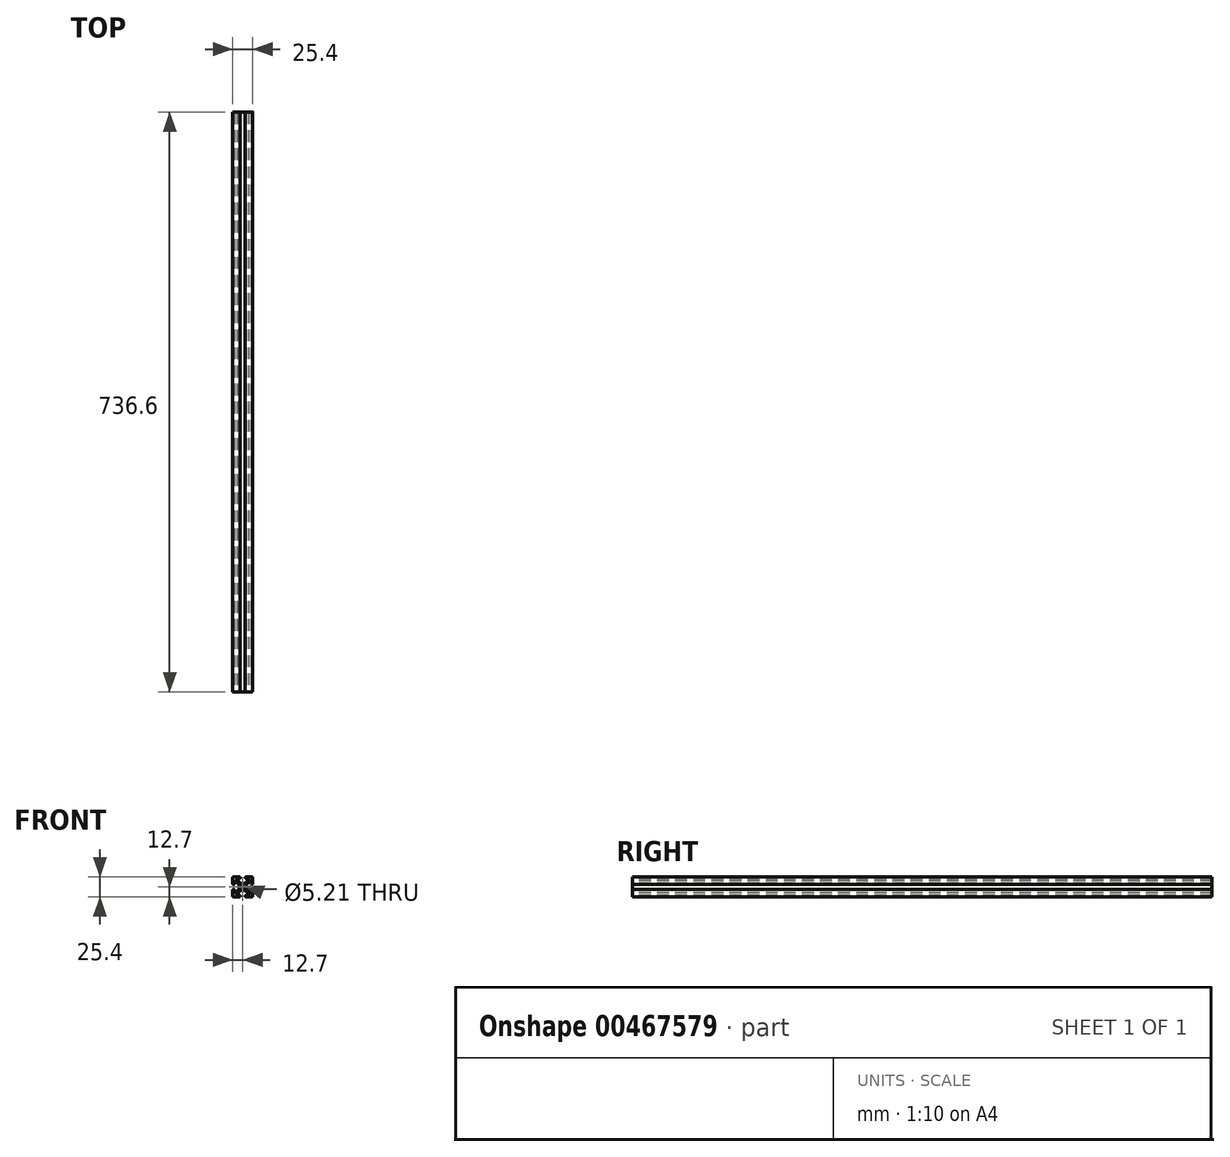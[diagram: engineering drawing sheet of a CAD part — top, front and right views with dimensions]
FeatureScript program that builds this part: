
annotation { "Feature Type Name" : "Feature", "Feature Type Description" : "" }
export const myFeature = defineFeature(function(context is Context, id is Id, definition is map)
    precondition{}
    {
        {
            var Q0;
            Q0=qCreatedBy(makeId("Front.planeOp"),FACE);
            var sketch = newSketch(context, id + "F0", { "sketchPlane" : qUnion([Q0])});
            skLineSegment(sketch, "E0", {"start": v(0, 0) * mm, "end": v(0, 4.5) * mm});
            skLineSegment(sketch, "E1", {"start": v(0, 4.5) * mm, "end": v(-2.54, 4.5) * mm});
            skLineSegment(sketch, "E2", {"start": v(-3.31, 4.83) * mm, "end": v(-7.1, 8.63) * mm});
            skLineSegment(sketch, "E3", {"start": v(-6.34, 10.5) * mm, "end": v(-4.33, 10.5) * mm});
            skLineSegment(sketch, "E4", {"start": v(-3.24, 11.58) * mm, "end": v(-3.24, 11.6) * mm});
            skLineSegment(sketch, "E5", {"start": v(-4.33, 12.7) * mm, "end": v(-11.6, 12.7) * mm});
            skLineSegment(sketch, "E6", {"start": v(-12.7, 11.6) * mm, "end": v(-12.7, 4.34) * mm});
            skLineSegment(sketch, "E7", {"start": v(-11.6, 3.25) * mm, "end": v(-11.58, 3.25) * mm});
            skLineSegment(sketch, "E8", {"start": v(-10.5, 4.34) * mm, "end": v(-10.5, 6.24) * mm});
            skLineSegment(sketch, "E9", {"start": v(-8.63, 7.02) * mm, "end": v(-4.83, 3.22) * mm});
            skLineSegment(sketch, "E10", {"start": v(-4.5, 2.45) * mm, "end": v(-4.5, 0) * mm});
            skLineSegment(sketch, "E11", {"start": v(-4.5, 0) * mm, "end": v(0, 0) * mm});
            skPoint(sketch, "E12.visualSharp", {"position": v(-12.7, 12.7) * mm});
            skArc(sketch, "E12.filletArc", {"start": v(-11.6, 12.7) * mm, "mid": v(-12.38, 12.38) * mm, "end": v(-12.7, 11.6) * mm});
            skPoint(sketch, "E13.visualSharp", {"position": v(-10.5, 3.25) * mm});
            skArc(sketch, "E13.filletArc", {"start": v(-11.58, 3.25) * mm, "mid": v(-10.81, 3.57) * mm, "end": v(-10.5, 4.34) * mm});
            skPoint(sketch, "E14.visualSharp", {"position": v(-12.7, 3.25) * mm});
            skArc(sketch, "E14.filletArc", {"start": v(-12.7, 4.34) * mm, "mid": v(-12.38, 3.57) * mm, "end": v(-11.6, 3.25) * mm});
            skPoint(sketch, "E15.visualSharp", {"position": v(-3.24, 10.5) * mm});
            skArc(sketch, "E15.filletArc", {"start": v(-4.33, 10.5) * mm, "mid": v(-3.56, 10.81) * mm, "end": v(-3.24, 11.58) * mm});
            skPoint(sketch, "E16.visualSharp", {"position": v(-3.24, 12.7) * mm});
            skArc(sketch, "E16.filletArc", {"start": v(-3.24, 11.6) * mm, "mid": v(-3.56, 12.38) * mm, "end": v(-4.33, 12.7) * mm});
            skPoint(sketch, "E17.visualSharp", {"position": v(-8.97, 10.5) * mm});
            skArc(sketch, "E17.filletArc", {"start": v(-6.34, 10.5) * mm, "mid": v(-7.35, 9.82) * mm, "end": v(-7.1, 8.63) * mm});
            skPoint(sketch, "E18.visualSharp", {"position": v(-10.5, 8.88) * mm});
            skArc(sketch, "E18.filletArc", {"start": v(-8.63, 7.02) * mm, "mid": v(-9.82, 7.25) * mm, "end": v(-10.5, 6.24) * mm});
            skPoint(sketch, "E19.visualSharp", {"position": v(-4.5, 2.9) * mm});
            skArc(sketch, "E19.filletArc", {"start": v(-4.5, 2.45) * mm, "mid": v(-4.6, 2.87) * mm, "end": v(-4.83, 3.22) * mm});
            skPoint(sketch, "E20.visualSharp", {"position": v(-3, 4.5) * mm});
            skArc(sketch, "E20.filletArc", {"start": v(-3.31, 4.83) * mm, "mid": v(-2.96, 4.6) * mm, "end": v(-2.54, 4.5) * mm});
            skLineSegment(sketch, "E21.MirrorCS", {"start": v(3.24, 11.58) * mm, "end": v(3.24, 11.6) * mm});
            skArc(sketch, "E22.MirrorCS", {"start": v(12.7, 4.34) * mm, "mid": v(12.38, 3.57) * mm, "end": v(11.6, 3.25) * mm});
            skArc(sketch, "E23.MirrorCS", {"start": v(4.33, 10.5) * mm, "mid": v(3.56, 10.81) * mm, "end": v(3.24, 11.58) * mm});
            skLineSegment(sketch, "E24.MirrorCS", {"start": v(11.6, 3.25) * mm, "end": v(11.58, 3.25) * mm});
            skArc(sketch, "E25.MirrorCS", {"start": v(3.31, 4.83) * mm, "mid": v(2.96, 4.6) * mm, "end": v(2.54, 4.5) * mm});
            skArc(sketch, "E26.MirrorCS", {"start": v(4.5, 2.45) * mm, "mid": v(4.6, 2.87) * mm, "end": v(4.83, 3.22) * mm});
            skArc(sketch, "E27.MirrorCS", {"start": v(11.58, 3.25) * mm, "mid": v(10.81, 3.57) * mm, "end": v(10.5, 4.34) * mm});
            skArc(sketch, "E28.MirrorCS", {"start": v(3.24, 11.6) * mm, "mid": v(3.56, 12.38) * mm, "end": v(4.33, 12.7) * mm});
            skArc(sketch, "E29.MirrorCS", {"start": v(11.6, 12.7) * mm, "mid": v(12.38, 12.38) * mm, "end": v(12.7, 11.6) * mm});
            skArc(sketch, "E30.MirrorCS", {"start": v(8.63, 7.02) * mm, "mid": v(9.82, 7.25) * mm, "end": v(10.5, 6.24) * mm});
            skLineSegment(sketch, "E31.MirrorCS", {"start": v(4.5, 2.45) * mm, "end": v(4.5, 0) * mm});
            skLineSegment(sketch, "E32.MirrorCS", {"start": v(10.5, 4.34) * mm, "end": v(10.5, 6.24) * mm});
            skArc(sketch, "E33.MirrorCS", {"start": v(6.34, 10.5) * mm, "mid": v(7.35, 9.82) * mm, "end": v(7.1, 8.63) * mm});
            skLineSegment(sketch, "E34.MirrorCS", {"start": v(0, 4.5) * mm, "end": v(2.54, 4.5) * mm});
            skLineSegment(sketch, "E35.MirrorCS", {"start": v(6.34, 10.5) * mm, "end": v(4.33, 10.5) * mm});
            skLineSegment(sketch, "E36.MirrorCS", {"start": v(4.33, 12.7) * mm, "end": v(11.6, 12.7) * mm});
            skPoint(sketch, "E37.MirrorP", {"position": v(12.7, 3.25) * mm});
            skLineSegment(sketch, "E38.MirrorCS", {"start": v(4.5, 0) * mm, "end": v(0, 0) * mm});
            skPoint(sketch, "E39.MirrorP", {"position": v(12.7, 12.7) * mm});
            skPoint(sketch, "E40.MirrorP", {"position": v(3, 4.5) * mm});
            skPoint(sketch, "E41.MirrorP", {"position": v(10.5, 3.25) * mm});
            skLineSegment(sketch, "E42.MirrorCS", {"start": v(8.63, 7.02) * mm, "end": v(4.83, 3.22) * mm});
            skPoint(sketch, "E43.MirrorP", {"position": v(3.24, 10.5) * mm});
            skLineSegment(sketch, "E44.MirrorCS", {"start": v(12.7, 11.6) * mm, "end": v(12.7, 4.34) * mm});
            skPoint(sketch, "E45.MirrorP", {"position": v(4.5, 2.9) * mm});
            skPoint(sketch, "E46.MirrorP", {"position": v(10.5, 8.88) * mm});
            skPoint(sketch, "E47.MirrorP", {"position": v(8.97, 10.5) * mm});
            skPoint(sketch, "E48.MirrorP", {"position": v(3.24, 12.7) * mm});
            skLineSegment(sketch, "E49.MirrorCS", {"start": v(3.31, 4.83) * mm, "end": v(7.1, 8.63) * mm});
            skLineSegment(sketch, "E50.MirrorCS", {"start": v(-3.24, -11.58) * mm, "end": v(-3.24, -11.6) * mm});
            skArc(sketch, "E51.MirrorCS", {"start": v(-3.24, -11.6) * mm, "mid": v(-3.56, -12.38) * mm, "end": v(-4.33, -12.7) * mm});
            skArc(sketch, "E52.MirrorCS", {"start": v(-4.33, -10.5) * mm, "mid": v(-3.56, -10.81) * mm, "end": v(-3.24, -11.58) * mm});
            skLineSegment(sketch, "E53.MirrorCS", {"start": v(3.24, -11.58) * mm, "end": v(3.24, -11.6) * mm});
            skArc(sketch, "E54.MirrorCS", {"start": v(3.24, -11.6) * mm, "mid": v(3.56, -12.38) * mm, "end": v(4.33, -12.7) * mm});
            skLineSegment(sketch, "E55.MirrorCS", {"start": v(11.6, -3.25) * mm, "end": v(11.58, -3.25) * mm});
            skLineSegment(sketch, "E56.MirrorCS", {"start": v(0, -4.5) * mm, "end": v(2.54, -4.5) * mm});
            skArc(sketch, "E57.MirrorCS", {"start": v(-3.31, -4.83) * mm, "mid": v(-2.96, -4.6) * mm, "end": v(-2.54, -4.5) * mm});
            skArc(sketch, "E58.MirrorCS", {"start": v(12.7, -4.34) * mm, "mid": v(12.38, -3.57) * mm, "end": v(11.6, -3.25) * mm});
            skArc(sketch, "E59.MirrorCS", {"start": v(3.31, -4.83) * mm, "mid": v(2.96, -4.6) * mm, "end": v(2.54, -4.5) * mm});
            skArc(sketch, "E60.MirrorCS", {"start": v(11.58, -3.25) * mm, "mid": v(10.81, -3.57) * mm, "end": v(10.5, -4.34) * mm});
            skLineSegment(sketch, "E61.MirrorCS", {"start": v(-11.6, -3.25) * mm, "end": v(-11.58, -3.25) * mm});
            skLineSegment(sketch, "E62.MirrorCS", {"start": v(0, -4.5) * mm, "end": v(-2.54, -4.5) * mm});
            skArc(sketch, "E63.MirrorCS", {"start": v(-12.7, -4.34) * mm, "mid": v(-12.38, -3.57) * mm, "end": v(-11.6, -3.25) * mm});
            skArc(sketch, "E64.MirrorCS", {"start": v(-11.58, -3.25) * mm, "mid": v(-10.81, -3.57) * mm, "end": v(-10.5, -4.34) * mm});
            skArc(sketch, "E65.MirrorCS", {"start": v(-4.5, -2.45) * mm, "mid": v(-4.6, -2.87) * mm, "end": v(-4.83, -3.22) * mm});
            skArc(sketch, "E66.MirrorCS", {"start": v(4.5, -2.45) * mm, "mid": v(4.6, -2.87) * mm, "end": v(4.83, -3.22) * mm});
            skLineSegment(sketch, "E67.MirrorCS", {"start": v(10.5, -4.34) * mm, "end": v(10.5, -6.24) * mm});
            skArc(sketch, "E68.MirrorCS", {"start": v(-8.63, -7.02) * mm, "mid": v(-9.82, -7.25) * mm, "end": v(-10.5, -6.24) * mm});
            skArc(sketch, "E69.MirrorCS", {"start": v(11.6, -12.7) * mm, "mid": v(12.38, -12.38) * mm, "end": v(12.7, -11.6) * mm});
            skLineSegment(sketch, "E70.MirrorCS", {"start": v(4.5, -2.45) * mm, "end": v(4.5, 0) * mm});
            skArc(sketch, "E71.MirrorCS", {"start": v(4.33, -10.5) * mm, "mid": v(3.56, -10.81) * mm, "end": v(3.24, -11.58) * mm});
            skArc(sketch, "E72.MirrorCS", {"start": v(-11.6, -12.7) * mm, "mid": v(-12.38, -12.38) * mm, "end": v(-12.7, -11.6) * mm});
            skLineSegment(sketch, "E73.MirrorCS", {"start": v(-4.5, -2.45) * mm, "end": v(-4.5, 0) * mm});
            skLineSegment(sketch, "E74.MirrorCS", {"start": v(-10.5, -4.34) * mm, "end": v(-10.5, -6.24) * mm});
            skLineSegment(sketch, "E75.MirrorCS", {"start": v(-6.34, -10.5) * mm, "end": v(-4.33, -10.5) * mm});
            skArc(sketch, "E76.MirrorCS", {"start": v(6.34, -10.5) * mm, "mid": v(7.35, -9.82) * mm, "end": v(7.1, -8.63) * mm});
            skArc(sketch, "E77.MirrorCS", {"start": v(-6.34, -10.5) * mm, "mid": v(-7.35, -9.82) * mm, "end": v(-7.1, -8.63) * mm});
            skLineSegment(sketch, "E78.MirrorCS", {"start": v(6.34, -10.5) * mm, "end": v(4.33, -10.5) * mm});
            skArc(sketch, "E79.MirrorCS", {"start": v(8.63, -7.02) * mm, "mid": v(9.82, -7.25) * mm, "end": v(10.5, -6.24) * mm});
            skLineSegment(sketch, "E80.MirrorCS", {"start": v(-8.63, -7.02) * mm, "end": v(-4.83, -3.22) * mm});
            skLineSegment(sketch, "E81.MirrorCS", {"start": v(-4.33, -12.7) * mm, "end": v(-11.6, -12.7) * mm});
            skLineSegment(sketch, "E82.MirrorCS", {"start": v(4.33, -12.7) * mm, "end": v(11.6, -12.7) * mm});
            skLineSegment(sketch, "E83.MirrorCS", {"start": v(8.63, -7.02) * mm, "end": v(4.83, -3.22) * mm});
            skPoint(sketch, "E84.MirrorP", {"position": v(-4.5, -2.9) * mm});
            skPoint(sketch, "E85.MirrorP", {"position": v(10.5, -3.25) * mm});
            skLineSegment(sketch, "E86.MirrorCS", {"start": v(12.7, -11.6) * mm, "end": v(12.7, -4.34) * mm});
            skLineSegment(sketch, "E87.MirrorCS", {"start": v(-12.7, -11.6) * mm, "end": v(-12.7, -4.34) * mm});
            skPoint(sketch, "E88.MirrorP", {"position": v(-12.7, -12.7) * mm});
            skPoint(sketch, "E89.MirrorP", {"position": v(-3, -4.5) * mm});
            skPoint(sketch, "E90.MirrorP", {"position": v(4.5, -2.9) * mm});
            skPoint(sketch, "E91.MirrorP", {"position": v(-10.5, -3.25) * mm});
            skPoint(sketch, "E92.MirrorP", {"position": v(8.97, -10.5) * mm});
            skPoint(sketch, "E93.MirrorP", {"position": v(12.7, -3.25) * mm});
            skLineSegment(sketch, "E94.MirrorCS", {"start": v(-3.31, -4.83) * mm, "end": v(-7.1, -8.63) * mm});
            skPoint(sketch, "E95.MirrorP", {"position": v(-12.7, -3.25) * mm});
            skPoint(sketch, "E96.MirrorP", {"position": v(3, -4.5) * mm});
            skLineSegment(sketch, "E97.MirrorCS", {"start": v(0, 0) * mm, "end": v(0, -4.5) * mm});
            skPoint(sketch, "E98.MirrorP", {"position": v(-3.24, -10.5) * mm});
            skPoint(sketch, "E99.MirrorP", {"position": v(-3.24, -12.7) * mm});
            skPoint(sketch, "E100.MirrorP", {"position": v(-8.97, -10.5) * mm});
            skLineSegment(sketch, "E101.MirrorCS", {"start": v(3.31, -4.83) * mm, "end": v(7.1, -8.63) * mm});
            skPoint(sketch, "E102.MirrorP", {"position": v(3.24, -10.5) * mm});
            skPoint(sketch, "E103.MirrorP", {"position": v(10.5, -8.88) * mm});
            skPoint(sketch, "E104.MirrorP", {"position": v(-10.5, -8.88) * mm});
            skPoint(sketch, "E105.MirrorP", {"position": v(12.7, -12.7) * mm});
            skPoint(sketch, "E106.MirrorP", {"position": v(3.24, -12.7) * mm});
            skSolve(sketch);
        }
        {
            var Q0;
            Q0=makeQuery(id+"F0.imprint","IMPRINT",FACE,{"disambiguationData":[TD([[makeQuery(id+"F0.imprint","IMPRINT",EDGE,{"derivedFrom":sQuery(id+"F0.wireOp",EDGE,"E0")}),1.0]])]});
            var Q1;
            Q1=makeQuery(id+"F0.imprint","IMPRINT",FACE,{"disambiguationData":[TD([[makeQuery(id+"F0.imprint","IMPRINT",EDGE,{"derivedFrom":sQuery(id+"F0.wireOp",EDGE,"E0")}),-1.0]])]});
            var Q2;
            Q2=makeQuery(id+"F0.imprint","IMPRINT",FACE,{"disambiguationData":[TD([[makeQuery(id+"F0.imprint","IMPRINT",EDGE,{"derivedFrom":sQuery(id+"F0.wireOp",EDGE,"E53.MirrorCS")}),1.0]])]});
            var Q3;
            Q3=makeQuery(id+"F0.imprint","IMPRINT",FACE,{"disambiguationData":[TD([[makeQuery(id+"F0.imprint","IMPRINT",EDGE,{"derivedFrom":sQuery(id+"F0.wireOp",EDGE,"E11")}),-1.0]])]});
            extrude(context, id + "F1", {"entities" : qUnion([Q0, Q1, Q2, Q3]), "oppositeDirection" : true, "depth" : 736.6 * mm});
        }
        {
            var Q0;
            Q0=makeQuery(id+"F1.opExtrude","CAP_FACE",FACE,{"disambiguationData":[OSD([sQuery(id+"F0.wireOp",EDGE,"E1"),sQuery(id+"F0.wireOp",EDGE,"E2"),sQuery(id+"F0.wireOp",EDGE,"E3"),sQuery(id+"F0.wireOp",EDGE,"E4"),sQuery(id+"F0.wireOp",EDGE,"E5"),sQuery(id+"F0.wireOp",EDGE,"E6"),sQuery(id+"F0.wireOp",EDGE,"E7"),sQuery(id+"F0.wireOp",EDGE,"E8"),sQuery(id+"F0.wireOp",EDGE,"E9"),sQuery(id+"F0.wireOp",EDGE,"E10"),sQuery(id+"F0.wireOp",EDGE,"E12.filletArc"),sQuery(id+"F0.wireOp",EDGE,"E13.filletArc"),sQuery(id+"F0.wireOp",EDGE,"E14.filletArc"),sQuery(id+"F0.wireOp",EDGE,"E15.filletArc"),sQuery(id+"F0.wireOp",EDGE,"E16.filletArc"),sQuery(id+"F0.wireOp",EDGE,"E17.filletArc"),sQuery(id+"F0.wireOp",EDGE,"E18.filletArc"),sQuery(id+"F0.wireOp",EDGE,"E19.filletArc"),sQuery(id+"F0.wireOp",EDGE,"E20.filletArc"),sQuery(id+"F0.wireOp",EDGE,"E21.MirrorCS"),sQuery(id+"F0.wireOp",EDGE,"E22.MirrorCS"),sQuery(id+"F0.wireOp",EDGE,"E23.MirrorCS"),sQuery(id+"F0.wireOp",EDGE,"E24.MirrorCS"),sQuery(id+"F0.wireOp",EDGE,"E25.MirrorCS"),sQuery(id+"F0.wireOp",EDGE,"E26.MirrorCS"),sQuery(id+"F0.wireOp",EDGE,"E27.MirrorCS"),sQuery(id+"F0.wireOp",EDGE,"E28.MirrorCS"),sQuery(id+"F0.wireOp",EDGE,"E29.MirrorCS"),sQuery(id+"F0.wireOp",EDGE,"E30.MirrorCS"),sQuery(id+"F0.wireOp",EDGE,"E31.MirrorCS"),sQuery(id+"F0.wireOp",EDGE,"E32.MirrorCS"),sQuery(id+"F0.wireOp",EDGE,"E33.MirrorCS"),sQuery(id+"F0.wireOp",EDGE,"E34.MirrorCS"),sQuery(id+"F0.wireOp",EDGE,"E35.MirrorCS"),sQuery(id+"F0.wireOp",EDGE,"E36.MirrorCS"),sQuery(id+"F0.wireOp",EDGE,"E42.MirrorCS"),sQuery(id+"F0.wireOp",EDGE,"E44.MirrorCS"),sQuery(id+"F0.wireOp",EDGE,"E49.MirrorCS"),sQuery(id+"F0.wireOp",EDGE,"E50.MirrorCS"),sQuery(id+"F0.wireOp",EDGE,"E51.MirrorCS"),sQuery(id+"F0.wireOp",EDGE,"E52.MirrorCS"),sQuery(id+"F0.wireOp",EDGE,"E53.MirrorCS"),sQuery(id+"F0.wireOp",EDGE,"E54.MirrorCS"),sQuery(id+"F0.wireOp",EDGE,"E55.MirrorCS"),sQuery(id+"F0.wireOp",EDGE,"E56.MirrorCS"),sQuery(id+"F0.wireOp",EDGE,"E57.MirrorCS"),sQuery(id+"F0.wireOp",EDGE,"E58.MirrorCS"),sQuery(id+"F0.wireOp",EDGE,"E59.MirrorCS"),sQuery(id+"F0.wireOp",EDGE,"E60.MirrorCS"),sQuery(id+"F0.wireOp",EDGE,"E61.MirrorCS"),sQuery(id+"F0.wireOp",EDGE,"E62.MirrorCS"),sQuery(id+"F0.wireOp",EDGE,"E63.MirrorCS"),sQuery(id+"F0.wireOp",EDGE,"E64.MirrorCS"),sQuery(id+"F0.wireOp",EDGE,"E65.MirrorCS"),sQuery(id+"F0.wireOp",EDGE,"E66.MirrorCS"),sQuery(id+"F0.wireOp",EDGE,"E67.MirrorCS"),sQuery(id+"F0.wireOp",EDGE,"E68.MirrorCS"),sQuery(id+"F0.wireOp",EDGE,"E69.MirrorCS"),sQuery(id+"F0.wireOp",EDGE,"E70.MirrorCS"),sQuery(id+"F0.wireOp",EDGE,"E71.MirrorCS"),sQuery(id+"F0.wireOp",EDGE,"E72.MirrorCS"),sQuery(id+"F0.wireOp",EDGE,"E73.MirrorCS"),sQuery(id+"F0.wireOp",EDGE,"E74.MirrorCS"),sQuery(id+"F0.wireOp",EDGE,"E75.MirrorCS"),sQuery(id+"F0.wireOp",EDGE,"E76.MirrorCS"),sQuery(id+"F0.wireOp",EDGE,"E77.MirrorCS"),sQuery(id+"F0.wireOp",EDGE,"E78.MirrorCS"),sQuery(id+"F0.wireOp",EDGE,"E79.MirrorCS"),sQuery(id+"F0.wireOp",EDGE,"E80.MirrorCS"),sQuery(id+"F0.wireOp",EDGE,"E81.MirrorCS"),sQuery(id+"F0.wireOp",EDGE,"E82.MirrorCS"),sQuery(id+"F0.wireOp",EDGE,"E83.MirrorCS"),sQuery(id+"F0.wireOp",EDGE,"E86.MirrorCS"),sQuery(id+"F0.wireOp",EDGE,"E87.MirrorCS"),sQuery(id+"F0.wireOp",EDGE,"E94.MirrorCS"),sQuery(id+"F0.wireOp",EDGE,"E101.MirrorCS")])],"isStart":true});
            var sketch = newSketch(context, id + "F2", { "sketchPlane" : qUnion([Q0])});
            skCircle(sketch, "E107", {"center": v(0, 0) * mm, "radius": 2.6 * mm});
            skSolve(sketch);
        }
        {
            var Q0;
            Q0 = qSketchRegion(id + "F2", true);
            extrude(context, id + "F3", {"entities" : qUnion([Q0]), "operationType" : NewBodyOperationType.REMOVE, "endBound" : BoundingType.THROUGH_ALL, "oppositeDirection" : true, "depth" : 25.4 * mm});
        }
    });
